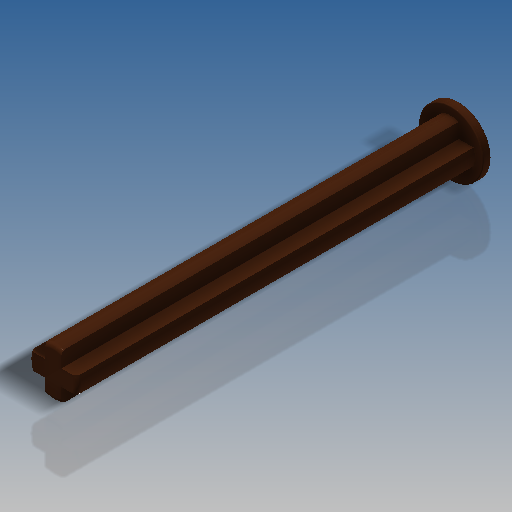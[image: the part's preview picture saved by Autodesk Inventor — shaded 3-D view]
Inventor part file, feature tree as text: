
AUTODESK INVENTOR PART (.ipt)
format: ipt  version: 2019.4 (Build 234330000, 330)  size: 201,728 bytes
history: native  units: in
note: dims shown in document units (in); Inventor stores cm internally (conversion verified against a paired STEP export)
features: extrude x2, sketch x2, fillet x1
ambient origin geometry x8: Origin, YZ Plane, XZ Plane, XY Plane, X Axis, Y Axis, Z Axis, Center Point
bodies: Solid1 (feature_tree)
feature tree (5):
  extrude  "Extrusion1"  Depth=0.063in
  extrude  "Extrusion2"  TaperAngle=0.0deg  [1 undecoded]
  fillet  "Fillet1"  Radius=0.0157in
  sketch  "Sketch1"  dims[d0=0.189in d1=0.063in]
  sketch  "Sketch2"  dims[d2=1.5748in d3=0.0in d4=0.0157in d7=0.252in d8=0.0315in d9=0.0in d10=0.0039in d11=0.0in d12=0.0in]
note: 1 required parameter value undecoded (feature->parameter linkage not recoverable at this tier; creation-order binding heuristic only, values carry confidence <= 0.55)
